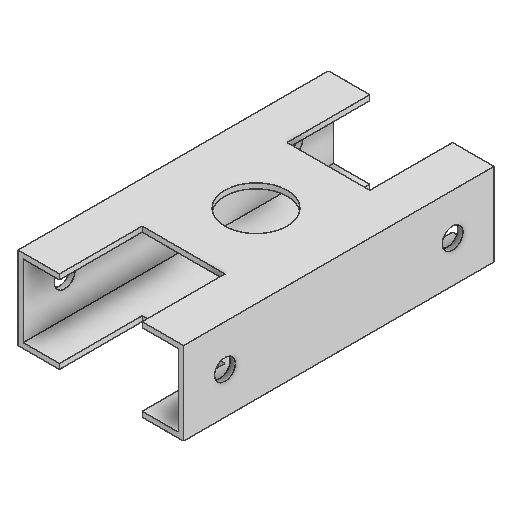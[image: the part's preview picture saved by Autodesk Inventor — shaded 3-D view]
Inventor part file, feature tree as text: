
AUTODESK INVENTOR PART (.ipt)
format: ipt  version: 2025.2 (Build 292293000, 293)  size: 164,864 bytes
history: native  units: in
note: dims shown in document units (in); Inventor stores cm internally (conversion verified against a paired STEP export)
features: extrude x3, sketch x3
ambient origin geometry x8: Origin, YZ Plane, XZ Plane, XY Plane, X Axis, Y Axis, Z Axis, Center Point
bodies: Solid1 (feature_tree)
feature tree (6):
  extrude  "Extrusion1"  Depth=1.0in
  extrude  "Extrusion2"  Depth=0.0625in
  extrude  "Extrusion3"  Depth=0.0625in
  sketch  "Sketch1"  dims[d0=2.0in d1=1.0in]
  sketch  "Sketch2"  dims[d2=0.0625in d3=0.0625in]
  sketch  "Sketch3"  dims[d4=0.0625in d5=0.0625in d6=3.75in d7=0.0in d8=0.75in d9=1.0in d10=1.875in d11=4.6in d12=0.0in d13=1.0in d14=1.0in d15=1.0in d16=1.0in d17=0.25in d18=0.5in d19=0.5in d20=0.25in d21=0.5in d22=0.5in d23=0.0in d24=0.0in d25=3.75in]
